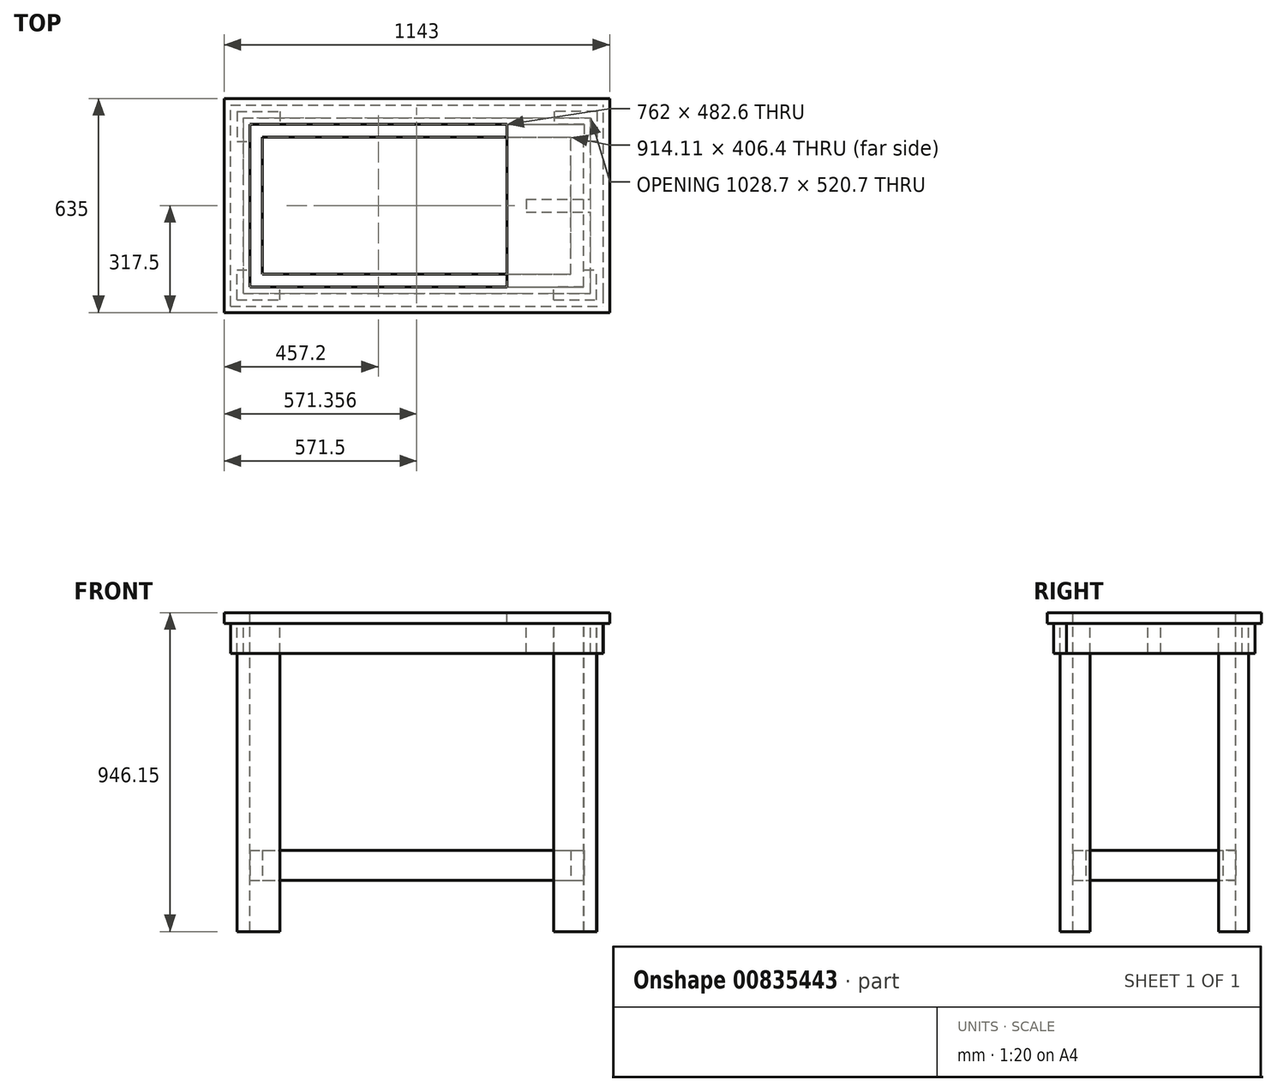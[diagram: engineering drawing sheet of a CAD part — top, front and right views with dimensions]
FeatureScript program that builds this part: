
annotation { "Feature Type Name" : "Feature", "Feature Type Description" : "" }
export const myFeature = defineFeature(function(context is Context, id is Id, definition is map)
    precondition{}
    {
        {
            var Q0;
            Q0=qCreatedBy(makeId("Top.planeOp"),FACE);
            var sketch = newSketch(context, id + "F0", { "sketchPlane" : qUnion([Q0])});
            skLineSegment(sketch, "E0.bottom", {"start": v(571.5, 317.5) * mm, "end": v(-571.5, 317.5) * mm});
            skLineSegment(sketch, "E0.top", {"start": v(571.5, -317.5) * mm, "end": v(-571.5, -317.5) * mm});
            skLineSegment(sketch, "E0.left", {"start": v(571.5, 317.5) * mm, "end": v(571.5, -317.5) * mm});
            skLineSegment(sketch, "E0.right", {"start": v(-571.5, 317.5) * mm, "end": v(-571.5, -317.5) * mm});
            skPoint(sketch, "E0.middle", {"position": v(0, 0) * mm});
            skSolve(sketch);
        }
        {
            var Q0;
            Q0=makeQuery(id+"F0.imprint","IMPRINT",FACE,{"disambiguationData":[TD([[makeQuery(id+"F0.imprint","IMPRINT",EDGE,{"derivedFrom":sQuery(id+"F0.wireOp",EDGE,"E0.bottom")}),1.0]])]});
            var sketch = newSketch(context, id + "F1", { "sketchPlane" : qUnion([Q0])});
            skLineSegment(sketch, "E1.bottom", {"start": v(-495.3, 241.3) * mm, "end": v(266.7, 241.3) * mm});
            skLineSegment(sketch, "E1.top", {"start": v(-495.3, -241.3) * mm, "end": v(266.7, -241.3) * mm});
            skLineSegment(sketch, "E1.left", {"start": v(-495.3, 241.3) * mm, "end": v(-495.3, -241.3) * mm});
            skLineSegment(sketch, "E1.right", {"start": v(266.7, 241.3) * mm, "end": v(266.7, -241.3) * mm});
            skSolve(sketch);
        }
        {
            var Q0;
            Q0=makeQuery(id+"F0.imprint","IMPRINT",FACE,{"disambiguationData":[TD([[makeQuery(id+"F0.imprint","IMPRINT",EDGE,{"derivedFrom":sQuery(id+"F0.wireOp",EDGE,"E0.bottom")}),1.0]])]});
            var sketch = newSketch(context, id + "F2", { "sketchPlane" : qUnion([Q0])});
            skSolve(sketch);
        }
        {
            var Q0;
            Q0=makeQuery(id+"F2.imprint","IMPRINT",FACE,{"disambiguationData":[TD([[makeQuery(id+"F2.imprint","IMPRINT",EDGE,{"derivedFrom":makeQuery(id+"F0.imprint","IMPRINT",EDGE,{"derivedFrom":sQuery(id+"F0.wireOp",EDGE,"E0.bottom")})}),1.0]])]});
            extrude(context, id + "F3", {"entities" : qUnion([Q0]), "oppositeDirection" : true, "depth" : 31.75 * mm, "offsetDistance" : 25.4 * mm});
        }
        {
            var Q0;
            Q0=makeQuery(id+"F1.imprint","IMPRINT",FACE,{"disambiguationData":[TD([[makeQuery(id+"F1.imprint","IMPRINT",EDGE,{"derivedFrom":sQuery(id+"F1.wireOp",EDGE,"E1.bottom")}),-1.0]])]});
            extrude(context, id + "F4", {"entities" : qUnion([Q0]), "operationType" : NewBodyOperationType.REMOVE, "endBound" : BoundingType.THROUGH_ALL, "oppositeDirection" : true, "depth" : 25.4 * mm, "offsetDistance" : 25.4 * mm});
        }
        {
            var Q0;
            Q0=makeQuery(id+"F3.opExtrude","CAP_FACE",FACE,{"disambiguationData":[OSD([sQuery(id+"F0.wireOp",EDGE,"E0.bottom"),sQuery(id+"F0.wireOp",EDGE,"E0.top"),sQuery(id+"F0.wireOp",EDGE,"E0.left"),sQuery(id+"F0.wireOp",EDGE,"E0.right")])],"isStart":false});
            var sketch = newSketch(context, id + "F5", { "sketchPlane" : qUnion([Q0])});
            skLineSegment(sketch, "E2.bottom", {"start": v(-552.45, 260.35) * mm, "end": v(-514.35, 260.35) * mm});
            skLineSegment(sketch, "E2.top", {"start": v(-552.45, -298.45) * mm, "end": v(-514.35, -298.45) * mm});
            skLineSegment(sketch, "E2.left", {"start": v(-552.45, 260.35) * mm, "end": v(-552.45, -298.45) * mm});
            skLineSegment(sketch, "E2.right", {"start": v(-514.35, 260.35) * mm, "end": v(-514.35, -298.45) * mm});
            skLineSegment(sketch, "E3.bottom", {"start": v(514.35, 260.35) * mm, "end": v(552.45, 260.35) * mm});
            skLineSegment(sketch, "E3.top", {"start": v(514.35, -298.45) * mm, "end": v(552.45, -298.45) * mm});
            skLineSegment(sketch, "E3.left", {"start": v(514.35, 260.35) * mm, "end": v(514.35, -298.45) * mm});
            skLineSegment(sketch, "E3.right", {"start": v(552.45, 260.35) * mm, "end": v(552.45, -298.45) * mm});
            skLineSegment(sketch, "E4.bottom", {"start": v(-552.45, 260.35) * mm, "end": v(552.16, 260.35) * mm});
            skLineSegment(sketch, "E4.top", {"start": v(-552.45, 298.45) * mm, "end": v(552.16, 298.45) * mm});
            skLineSegment(sketch, "E4.left", {"start": v(-552.45, 260.35) * mm, "end": v(-552.45, 298.45) * mm});
            skLineSegment(sketch, "E4.right", {"start": v(552.16, 260.35) * mm, "end": v(552.16, 298.45) * mm});
            skLineSegment(sketch, "E5.bottom", {"start": v(-514.35, -298.45) * mm, "end": v(515.62, -298.45) * mm});
            skLineSegment(sketch, "E5.top", {"start": v(-514.35, -260.35) * mm, "end": v(515.62, -260.35) * mm});
            skLineSegment(sketch, "E5.left", {"start": v(-514.35, -298.45) * mm, "end": v(-514.35, -260.35) * mm});
            skLineSegment(sketch, "E5.right", {"start": v(515.62, -298.45) * mm, "end": v(515.62, -260.35) * mm});
            skLineSegment(sketch, "E6.bottom", {"start": v(323.85, 260.35) * mm, "end": v(372.08, 260.35) * mm});
            skLineSegment(sketch, "E6.top", {"start": v(323.85, 260.35) * mm, "end": v(372.08, 260.35) * mm});
            skLineSegment(sketch, "E6.left", {"start": v(372.08, 260.35) * mm, "end": v(372.08, 260.35) * mm});
            skLineSegment(sketch, "E6.right", {"start": v(323.85, 260.35) * mm, "end": v(323.85, 260.35) * mm});
            skLineSegment(sketch, "E7.bottom", {"start": v(285.75, -260.35) * mm, "end": v(323.85, -260.35) * mm});
            skLineSegment(sketch, "E7.top", {"start": v(285.75, 260.35) * mm, "end": v(323.85, 260.35) * mm});
            skLineSegment(sketch, "E7.left", {"start": v(285.75, -260.35) * mm, "end": v(285.75, 260.35) * mm});
            skLineSegment(sketch, "E7.right", {"start": v(323.85, -260.35) * mm, "end": v(323.85, 260.35) * mm});
            skLineSegment(sketch, "E8.bottom", {"start": v(323.85, -19.05) * mm, "end": v(514.35, -19.05) * mm});
            skLineSegment(sketch, "E8.top", {"start": v(323.85, 19.05) * mm, "end": v(514.35, 19.05) * mm});
            skLineSegment(sketch, "E8.left", {"start": v(323.85, -19.05) * mm, "end": v(323.85, 19.05) * mm});
            skLineSegment(sketch, "E8.right", {"start": v(514.35, -19.05) * mm, "end": v(514.35, 19.05) * mm});
            skSolve(sketch);
        }
        {
            var Q0;
            Q0 = qSketchRegion(id + "F5", true);
            var Q1;
            Q1=makeQuery(id+"F5.imprint","IMPRINT",FACE,{"disambiguationData":[TD([[makeQuery(id+"F5.imprint","IMPRINT",EDGE,{"derivedFrom":sQuery(id+"F5.wireOp",EDGE,"E7.bottom")}),1.0]])]});
            var Q2;
            Q2=makeQuery(id+"F5.imprint","IMPRINT",FACE,{"disambiguationData":[TD([[makeQuery(id+"F5.imprint","IMPRINT",EDGE,{"derivedFrom":sQuery(id+"F5.wireOp",EDGE,"E8.bottom")}),1.0]])]});
            extrude(context, id + "F6", {"entities" : qUnion([Q0, Q1, Q2]), "depth" : 88.9 * mm, "offsetDistance" : 25.4 * mm});
        }
        {
            var Q0;
            Q0=makeQuery(id+"F3.opExtrude","CAP_FACE",FACE,{"disambiguationData":[OSD([sQuery(id+"F0.wireOp",EDGE,"E0.bottom"),sQuery(id+"F0.wireOp",EDGE,"E0.top"),sQuery(id+"F0.wireOp",EDGE,"E0.left"),sQuery(id+"F0.wireOp",EDGE,"E0.right")])],"isStart":false});
            var sketch = newSketch(context, id + "F7", { "sketchPlane" : qUnion([Q0])});
            skLineSegment(sketch, "E9.bottom", {"start": v(-533.4, 279.4) * mm, "end": v(-495.3, 279.4) * mm});
            skLineSegment(sketch, "E9.top", {"start": v(-533.4, 190.5) * mm, "end": v(-495.3, 190.5) * mm});
            skLineSegment(sketch, "E9.left", {"start": v(-533.4, 279.4) * mm, "end": v(-533.4, 190.5) * mm});
            skLineSegment(sketch, "E9.right", {"start": v(-495.3, 279.4) * mm, "end": v(-495.3, 190.5) * mm});
            skLineSegment(sketch, "E10.bottom", {"start": v(-495.3, 279.4) * mm, "end": v(-406.4, 279.4) * mm});
            skLineSegment(sketch, "E10.top", {"start": v(-495.3, 241.3) * mm, "end": v(-406.4, 241.3) * mm});
            skLineSegment(sketch, "E10.left", {"start": v(-495.3, 279.4) * mm, "end": v(-495.3, 241.3) * mm});
            skLineSegment(sketch, "E10.right", {"start": v(-406.4, 279.4) * mm, "end": v(-406.4, 241.3) * mm});
            skLineSegment(sketch, "E11.bottom", {"start": v(495.01, 279.4) * mm, "end": v(533.11, 279.4) * mm});
            skLineSegment(sketch, "E11.top", {"start": v(495.01, 190.5) * mm, "end": v(533.11, 190.5) * mm});
            skLineSegment(sketch, "E11.left", {"start": v(495.01, 279.4) * mm, "end": v(495.01, 190.5) * mm});
            skLineSegment(sketch, "E11.right", {"start": v(533.11, 279.4) * mm, "end": v(533.11, 190.5) * mm});
            skLineSegment(sketch, "E12.bottom", {"start": v(495.01, 279.4) * mm, "end": v(406.11, 279.4) * mm});
            skLineSegment(sketch, "E12.top", {"start": v(495.01, 241.3) * mm, "end": v(406.11, 241.3) * mm});
            skLineSegment(sketch, "E12.left", {"start": v(495.01, 279.4) * mm, "end": v(495.01, 241.3) * mm});
            skLineSegment(sketch, "E12.right", {"start": v(406.11, 279.4) * mm, "end": v(406.11, 241.3) * mm});
            skLineSegment(sketch, "E13.bottom", {"start": v(533.4, -279.4) * mm, "end": v(495.3, -279.4) * mm});
            skLineSegment(sketch, "E13.top", {"start": v(533.4, -190.5) * mm, "end": v(495.3, -190.5) * mm});
            skLineSegment(sketch, "E13.left", {"start": v(533.4, -279.4) * mm, "end": v(533.4, -190.5) * mm});
            skLineSegment(sketch, "E13.right", {"start": v(495.3, -279.4) * mm, "end": v(495.3, -190.5) * mm});
            skLineSegment(sketch, "E14.bottom", {"start": v(495.3, -279.4) * mm, "end": v(406.4, -279.4) * mm});
            skLineSegment(sketch, "E14.top", {"start": v(495.3, -241.3) * mm, "end": v(406.4, -241.3) * mm});
            skLineSegment(sketch, "E14.left", {"start": v(495.3, -279.4) * mm, "end": v(495.3, -241.3) * mm});
            skLineSegment(sketch, "E14.right", {"start": v(406.4, -279.4) * mm, "end": v(406.4, -241.3) * mm});
            skLineSegment(sketch, "E15.bottom", {"start": v(-533.4, -279.4) * mm, "end": v(-495.3, -279.4) * mm});
            skLineSegment(sketch, "E15.top", {"start": v(-533.4, -190.5) * mm, "end": v(-495.3, -190.5) * mm});
            skLineSegment(sketch, "E15.left", {"start": v(-533.4, -279.4) * mm, "end": v(-533.4, -190.5) * mm});
            skLineSegment(sketch, "E15.right", {"start": v(-495.3, -279.4) * mm, "end": v(-495.3, -190.5) * mm});
            skLineSegment(sketch, "E16.bottom", {"start": v(-495.3, -279.4) * mm, "end": v(-406.4, -279.4) * mm});
            skLineSegment(sketch, "E16.top", {"start": v(-495.3, -241.3) * mm, "end": v(-406.4, -241.3) * mm});
            skLineSegment(sketch, "E16.left", {"start": v(-495.3, -279.4) * mm, "end": v(-495.3, -241.3) * mm});
            skLineSegment(sketch, "E16.right", {"start": v(-406.4, -279.4) * mm, "end": v(-406.4, -241.3) * mm});
            skSolve(sketch);
        }
        {
            var Q0;
            Q0 = qSketchRegion(id + "F7", true);
            extrude(context, id + "F8", {"entities" : qUnion([Q0]), "depth" : 914.4 * mm, "offsetDistance" : 25.4 * mm});
        }
        {
            var Q0;
            Q0=makeQuery(id+"F0.imprint","IMPRINT",FACE,{"disambiguationData":[TD([[makeQuery(id+"F0.imprint","IMPRINT",EDGE,{"derivedFrom":sQuery(id+"F0.wireOp",EDGE,"E0.bottom")}),1.0]])]});
            var Q1;
            Q1=makeQuery(id+"F8.opExtrude","CAP_VERTEX",VERTEX,{"disambiguationData":[OSD([sQuery(id+"F7.wireOp",EDGE,"E10.bottom"),sQuery(id+"F7.wireOp",EDGE,"E10.right")])],"isStart":false});
            cPlane(context, id + "F9", {"entities" : qUnion([Q0, Q1]), "cplaneType" : CPlaneType.PLANE_POINT, "offset" : 25.4 * mm, "width" : 152.4 * mm, "height" : 152.4 * mm});
        }
        {
            var Q0;
            Q0=qCreatedBy(id+"F9.planeOp",FACE);
            cPlane(context, id + "F10", {"entities" : qUnion([Q0]), "cplaneType" : CPlaneType.OFFSET, "offset" : 152.4 * mm, "width" : 152.4 * mm, "height" : 152.4 * mm});
        }
        {
            var Q0;
            Q0=qCreatedBy(id+"F10.planeOp",FACE);
            var sketch = newSketch(context, id + "F11", { "sketchPlane" : qUnion([Q0])});
            skPoint(sketch, "E17", {"position": v(-495.3, -241.3) * mm});
            skPoint(sketch, "E18", {"position": v(495.01, -203.2) * mm});
            skLineSegment(sketch, "E19.bottom", {"start": v(-495.3, -241.3) * mm, "end": v(495.01, -241.3) * mm});
            skLineSegment(sketch, "E19.top", {"start": v(-495.3, -203.2) * mm, "end": v(495.01, -203.2) * mm});
            skLineSegment(sketch, "E19.left", {"start": v(-495.3, -241.3) * mm, "end": v(-495.3, -203.2) * mm});
            skLineSegment(sketch, "E19.right", {"start": v(495.01, -241.3) * mm, "end": v(495.01, -203.2) * mm});
            skPoint(sketch, "E20", {"position": v(-495.3, 241.3) * mm});
            skPoint(sketch, "E21", {"position": v(495.3, 203.2) * mm});
            skLineSegment(sketch, "E22.bottom", {"start": v(-495.3, 241.3) * mm, "end": v(495.3, 241.3) * mm});
            skLineSegment(sketch, "E22.top", {"start": v(-495.3, 203.2) * mm, "end": v(495.3, 203.2) * mm});
            skLineSegment(sketch, "E22.left", {"start": v(-495.3, 241.3) * mm, "end": v(-495.3, 203.2) * mm});
            skLineSegment(sketch, "E22.right", {"start": v(495.3, 241.3) * mm, "end": v(495.3, 203.2) * mm});
            skLineSegment(sketch, "E23.bottom", {"start": v(-495.3, -203.2) * mm, "end": v(-457.2, -203.2) * mm});
            skLineSegment(sketch, "E23.top", {"start": v(-495.3, 203.2) * mm, "end": v(-457.2, 203.2) * mm});
            skLineSegment(sketch, "E23.left", {"start": v(-495.3, -203.2) * mm, "end": v(-495.3, 203.2) * mm});
            skLineSegment(sketch, "E23.right", {"start": v(-457.2, -203.2) * mm, "end": v(-457.2, 203.2) * mm});
            skLineSegment(sketch, "E24.bottom", {"start": v(495.01, -203.2) * mm, "end": v(456.91, -203.2) * mm});
            skLineSegment(sketch, "E24.top", {"start": v(495.01, 203.2) * mm, "end": v(456.91, 203.2) * mm});
            skLineSegment(sketch, "E24.left", {"start": v(495.01, -203.2) * mm, "end": v(495.01, 203.2) * mm});
            skLineSegment(sketch, "E24.right", {"start": v(456.91, -203.2) * mm, "end": v(456.91, 203.2) * mm});
            skSolve(sketch);
        }
        {
            var Q0;
            Q0 = qSketchRegion(id + "F11", true);
            extrude(context, id + "F12", {"entities" : qUnion([Q0]), "depth" : 88.9 * mm, "offsetDistance" : 25.4 * mm});
        }
    });
